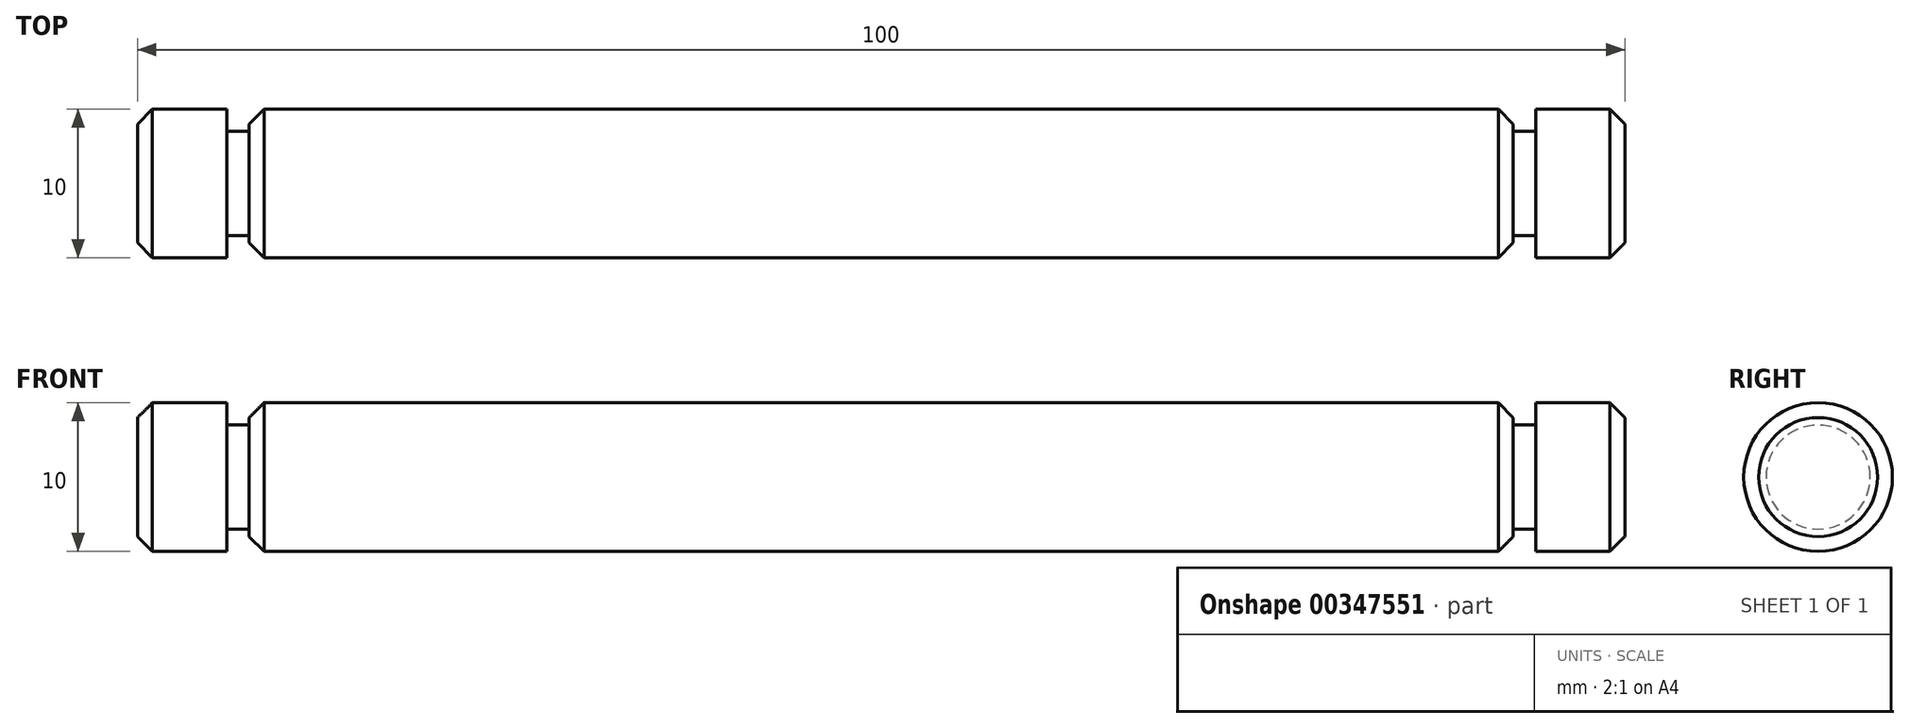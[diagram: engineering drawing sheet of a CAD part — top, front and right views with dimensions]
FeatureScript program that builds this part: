
annotation { "Feature Type Name" : "Feature", "Feature Type Description" : "" }
export const myFeature = defineFeature(function(context is Context, id is Id, definition is map)
    precondition{}
    {
        {
            var Q0;
            Q0=qCreatedBy(makeId("Front.planeOp"),FACE);
            var sketch = newSketch(context, id + "F0", { "sketchPlane" : qUnion([Q0])});
            skLineSegment(sketch, "E0", {"start": v(-83.15, 0) * mm, "end": v(16.85, 0) * mm});
            skLineSegment(sketch, "E1.0", {"start": v(-83.15, 5) * mm, "end": v(-77.15, 5) * mm});
            skLineSegment(sketch, "E2.0", {"start": v(-75.65, 5) * mm, "end": v(9.35, 5) * mm});
            skLineSegment(sketch, "E3", {"start": v(16.85, 5) * mm, "end": v(16.85, 0) * mm});
            skLineSegment(sketch, "E4.0", {"start": v(10.85, 5) * mm, "end": v(10.85, 3.5) * mm});
            skLineSegment(sketch, "E5", {"start": v(-83.15, 0) * mm, "end": v(-83.15, 5) * mm});
            skLineSegment(sketch, "E6.0", {"start": v(-77.15, 3.5) * mm, "end": v(-77.15, 5) * mm});
            skLineSegment(sketch, "E7.0", {"start": v(-75.65, 3.5) * mm, "end": v(-75.65, 5) * mm});
            skLineSegment(sketch, "E8.0", {"start": v(9.35, 5) * mm, "end": v(9.35, 3.5) * mm});
            skLineSegment(sketch, "E9.0", {"start": v(-77.15, 3.5) * mm, "end": v(-75.65, 3.5) * mm});
            skLineSegment(sketch, "E10.trimOffspring", {"start": v(9.35, 3.5) * mm, "end": v(10.85, 3.5) * mm});
            skLineSegment(sketch, "E11.trimOffspring", {"start": v(10.85, 5) * mm, "end": v(16.85, 5) * mm});
            skSolve(sketch);
        }
        {
            var Q0;
            Q0=makeQuery(id+"F0.imprint","IMPRINT",FACE,{"disambiguationData":[TD([[makeQuery(id+"F0.imprint","IMPRINT",EDGE,{"derivedFrom":sQuery(id+"F0.wireOp",EDGE,"E0")}),1.0]])]});
            var Q1;
            Q1=sQuery(id+"F0.wireOp",EDGE,"E0");
            revolve(context, id + "F1", {"entities" : qUnion([Q0]), "axis" : qUnion([Q1]), "revolveType" : RevolveType.FULL});
        }
        {
            var Q0;
            Q0=makeQuery(id+"F1.opRevolve","SWEPT_EDGE",EDGE,{"disambiguationData":[OSD([sQuery(id+"F0.wireOp",EDGE,"E1.0"),sQuery(id+"F0.wireOp",EDGE,"E5")])]});
            var Q1;
            Q1=makeQuery(id+"F1.opRevolve","SWEPT_EDGE",EDGE,{"disambiguationData":[OSD([sQuery(id+"F0.wireOp",EDGE,"E2.0"),sQuery(id+"F0.wireOp",EDGE,"E7.0")])]});
            var Q2;
            Q2=makeQuery(id+"F1.opRevolve","SWEPT_EDGE",EDGE,{"disambiguationData":[OSD([sQuery(id+"F0.wireOp",EDGE,"E3"),sQuery(id+"F0.wireOp",EDGE,"E11.trimOffspring")])]});
            var Q3;
            Q3=makeQuery(id+"F1.opRevolve","SWEPT_EDGE",EDGE,{"disambiguationData":[OSD([sQuery(id+"F0.wireOp",EDGE,"E2.0"),sQuery(id+"F0.wireOp",EDGE,"E8.0")])]});
            chamfer(context, id + "F2", {"entities" : qUnion([Q0, Q1, Q2, Q3]), "width" : 1 * mm, "tangentPropagation" : true});
        }
    });
